# Revit family: Echo Eliminator - Ceiling Baffles
name_source: partatom
category: Specialty Equipment
units: mm (PartAtom-declared; Revit-internal decimal feet)

## family parameters
Always vertical = Yes
Cut with Voids When Loaded = No
Enable Cutting in Views = Yes
Maintain Annotation Orientation = No
OmniClass Number = 23.35.00.00
OmniClass Title = Covering, Cladding, and Finishes
Part Type = Normal
Room Calculation Point = No
Round Connector Dimension = Use Diameter
Shared = No
Work Plane-Based = No

## types (46) — shared parameters
Acoustics - NRC = Sound absorption varies from NRC 0.45 to 0.95 based on installation method used when tested per ASTM C423.
Assembly Code = C30
Default Elevation = 0' - 0"
Description = Acoustic Panels
Fire Rating = ASTM E84 - Class A
Manufacturer = Acoustical Surfaces, Inc.
Material = Echo Eliminator
Model = Echo Eliminator - Baffles
Recycled Content Percentage = 0%
Type Comments = Acoustic panels for ceiling
URL = https://www.acousticalsurfaces.com

## per-type parameters (varying)
| type | B | Finish | Length | T | Thickness Options | Width | ‍      1. Thickness 1" | ‍      2. Thickness 2" |
| 24 x 48 - 1 INCH - Black | 1' - 0" | Paint - Acoustical-Surfaces - Echo Eliminator - Black | 4' - 0" | 0' - 1" | 1 | 2' - 0" | Yes | No |
| 24 x 48 - 1 INCH - Charcoal | 1' - 0" | Paint - Acoustical-Surfaces - Echo Eliminator - Charcoal | 4' - 0" | 0' - 1" | 1 | 2' - 0" | Yes | No |
| 24 x 48 - 1 INCH - Gray | 1' - 0" | Paint - Acoustical-Surfaces - Echo Eliminator - Grey | 4' - 0" | 0' - 1" | 1 | 2' - 0" | Yes | No |
| 24 x 48 - 1 INCH - Marble Blue | 1' - 0" | Paint - Acoustical-Surfaces - Echo Eliminator - Marble Blue | 4' - 0" | 0' - 1" | 1 | 2' - 0" | Yes | No |
| 24 x 48 - 1 INCH - Beige | 1' - 0" | Paint - Acoustical-Surfaces - Echo Eliminator - Beige | 4' - 0" | 0' - 1" | 1 | 2' - 0" | Yes | No |
| 24 x 48 - 1 INCH - White | 1' - 0" | Paint - Acoustical-Surfaces - Echo Eliminator - White | 4' - 0" | 0' - 1" | 1 | 2' - 0" | Yes | No |
| 48 x 96 - 2 INCH - Black | 2' - 0" | Paint - Acoustical-Surfaces - Echo Eliminator - Black | 8' - 0" | 0' - 2" | 2 | 4' - 0" | No | Yes |
| 48 x 96 - 2 INCH - Charcoal | 2' - 0" | Paint - Acoustical-Surfaces - Echo Eliminator - Charcoal | 8' - 0" | 0' - 2" | 2 | 4' - 0" | No | Yes |
| 48 x 96 - 2 INCH - Marble Blue | 2' - 0" | Paint - Acoustical-Surfaces - Echo Eliminator - Marble Blue | 8' - 0" | 0' - 2" | 2 | 4' - 0" | No | Yes |
| 48 x 96 - 2 INCH - Beige | 2' - 0" | Paint - Acoustical-Surfaces - Echo Eliminator - Beige | 8' - 0" | 0' - 2" | 2 | 4' - 0" | No | Yes |
| 48 x 96 - 2 INCH - White | 2' - 0" | Paint - Acoustical-Surfaces - Echo Eliminator - White | 8' - 0" | 0' - 2" | 2 | 4' - 0" | No | Yes |
| 48 x 96 - 1 INCH - Black | 2' - 0" | Paint - Acoustical-Surfaces - Echo Eliminator - Black | 8' - 0" | 0' - 1" | 1 | 4' - 0" | Yes | No |
| 48 x 96 - 1 INCH - Charcoal | 2' - 0" | Paint - Acoustical-Surfaces - Echo Eliminator - Charcoal | 8' - 0" | 0' - 1" | 1 | 4' - 0" | Yes | No |
| 48 x 96 - 1 INCH - Marble Blue | 2' - 0" | Paint - Acoustical-Surfaces - Echo Eliminator - Marble Blue | 8' - 0" | 0' - 1" | 1 | 4' - 0" | Yes | No |
| 48 x 96 - 1 INCH - Beige | 2' - 0" | Paint - Acoustical-Surfaces - Echo Eliminator - Beige | 8' - 0" | 0' - 1" | 1 | 4' - 0" | Yes | No |
| 48 x 96 - 1 INCH - White | 2' - 0" | Paint - Acoustical-Surfaces - Echo Eliminator - White | 8' - 0" | 0' - 1" | 1 | 4' - 0" | Yes | No |
| 48 x 48 - 2 INCH - Black | 2' - 0" | Paint - Acoustical-Surfaces - Echo Eliminator - Black | 4' - 0" | 0' - 2" | 2 | 4' - 0" | No | Yes |
| 48 x 48 - 2 INCH - Charcoal | 2' - 0" | Paint - Acoustical-Surfaces - Echo Eliminator - Charcoal | 4' - 0" | 0' - 2" | 2 | 4' - 0" | No | Yes |
| 48 x 48 - 2 INCH - Gray | 2' - 0" | Paint - Acoustical-Surfaces - Echo Eliminator - Grey | 4' - 0" | 0' - 2" | 2 | 4' - 0" | No | Yes |
| 48 x 48 - 2 INCH - Marble Blue | 2' - 0" | Paint - Acoustical-Surfaces - Echo Eliminator - Marble Blue | 4' - 0" | 0' - 2" | 2 | 4' - 0" | No | Yes |
| 48 x 48 - 2 INCH - Beige | 2' - 0" | Paint - Acoustical-Surfaces - Echo Eliminator - Beige | 4' - 0" | 0' - 2" | 2 | 4' - 0" | No | Yes |
| 48 x 48 - 2 INCH - White | 2' - 0" | Paint - Acoustical-Surfaces - Echo Eliminator - White | 4' - 0" | 0' - 2" | 2 | 4' - 0" | No | Yes |
| 48 x 48 - 1 INCH - Black | 2' - 0" | Paint - Acoustical-Surfaces - Echo Eliminator - Black | 4' - 0" | 0' - 1" | 1 | 4' - 0" | Yes | No |
| 48 x 48 - 1 INCH - Charcoal | 2' - 0" | Paint - Acoustical-Surfaces - Echo Eliminator - Charcoal | 4' - 0" | 0' - 1" | 1 | 4' - 0" | Yes | No |
| 48 x 48 - 1 INCH - Gray | 2' - 0" | Paint - Acoustical-Surfaces - Echo Eliminator - Grey | 4' - 0" | 0' - 1" | 1 | 4' - 0" | Yes | No |
| 48 x 48 - 1 INCH - Marble Blue | 2' - 0" | Paint - Acoustical-Surfaces - Echo Eliminator - Marble Blue | 4' - 0" | 0' - 1" | 1 | 4' - 0" | Yes | No |
| 48 x 48 - 1 INCH - Beige | 2' - 0" | Paint - Acoustical-Surfaces - Echo Eliminator - Beige | 4' - 0" | 0' - 1" | 1 | 4' - 0" | Yes | No |
| 48 x 48 - 1 INCH - White | 2' - 0" | Paint - Acoustical-Surfaces - Echo Eliminator - White | 4' - 0" | 0' - 1" | 1 | 4' - 0" | Yes | No |
| 24 x 24 - 2 INCH - Black | 1' - 0" | Paint - Acoustical-Surfaces - Echo Eliminator - Black | 2' - 0" | 0' - 2" | 2 | 2' - 0" | No | Yes |
| 24 x 24 - 2 INCH - Charcoal | 1' - 0" | Paint - Acoustical-Surfaces - Echo Eliminator - Charcoal | 2' - 0" | 0' - 2" | 2 | 2' - 0" | No | Yes |
| 24 x 24 - 2 INCH - Gray | 1' - 0" | Paint - Acoustical-Surfaces - Echo Eliminator - Grey | 2' - 0" | 0' - 2" | 2 | 2' - 0" | No | Yes |
| 24 x 24 - 2 INCH - Marble Blue | 1' - 0" | Paint - Acoustical-Surfaces - Echo Eliminator - Marble Blue | 2' - 0" | 0' - 2" | 2 | 2' - 0" | No | Yes |
| 24 x 24 - 2 INCH - Beige | 1' - 0" | Paint - Acoustical-Surfaces - Echo Eliminator - Beige | 2' - 0" | 0' - 2" | 2 | 2' - 0" | No | Yes |
| 24 x 24 - 2 INCH - White | 1' - 0" | Paint - Acoustical-Surfaces - Echo Eliminator - White | 2' - 0" | 0' - 2" | 2 | 2' - 0" | No | Yes |
| 24 x 24 - 1 INCH - Black | 1' - 0" | Paint - Acoustical-Surfaces - Echo Eliminator - Black | 2' - 0" | 0' - 1" | 1 | 2' - 0" | Yes | No |
| 24 x 24 - 1 INCH - Charcoal | 1' - 0" | Paint - Acoustical-Surfaces - Echo Eliminator - Charcoal | 2' - 0" | 0' - 1" | 1 | 2' - 0" | Yes | No |
| 24 x 24 - 1 INCH - Gray | 1' - 0" | Paint - Acoustical-Surfaces - Echo Eliminator - Grey | 2' - 0" | 0' - 1" | 1 | 2' - 0" | Yes | No |
| 24 x 24 - 1 INCH - Marble Blue | 1' - 0" | Paint - Acoustical-Surfaces - Echo Eliminator - Marble Blue | 2' - 0" | 0' - 1" | 1 | 2' - 0" | Yes | No |
| 24 x 24 - 1 INCH - Beige | 1' - 0" | Paint - Acoustical-Surfaces - Echo Eliminator - Beige | 2' - 0" | 0' - 1" | 1 | 2' - 0" | Yes | No |
| 24 x 24 - 1 INCH - White | 1' - 0" | Paint - Acoustical-Surfaces - Echo Eliminator - White | 2' - 0" | 0' - 1" | 1 | 2' - 0" | Yes | No |
| 24 x 48 - 2 INCH - Black | 1' - 0" | Paint - Acoustical-Surfaces - Echo Eliminator - Black | 4' - 0" | 0' - 2" | 2 | 2' - 0" | No | Yes |
| 24 x 48 - 2 INCH - Charcoal | 1' - 0" | Paint - Acoustical-Surfaces - Echo Eliminator - Charcoal | 4' - 0" | 0' - 2" | 2 | 2' - 0" | No | Yes |
| 24 x 48 - 2 INCH - Gray | 1' - 0" | Paint - Acoustical-Surfaces - Echo Eliminator - Grey | 4' - 0" | 0' - 2" | 2 | 2' - 0" | No | Yes |
| 24 x 48 - 2 INCH - Marble Blue | 1' - 0" | Paint - Acoustical-Surfaces - Echo Eliminator - Marble Blue | 4' - 0" | 0' - 2" | 2 | 2' - 0" | No | Yes |
| 24 x 48 - 2 INCH - Beige | 1' - 0" | Paint - Acoustical-Surfaces - Echo Eliminator - Beige | 4' - 0" | 0' - 2" | 2 | 2' - 0" | No | Yes |
| 24 x 48 - 2 INCH - White | 1' - 0" | Paint - Acoustical-Surfaces - Echo Eliminator - White | 4' - 0" | 0' - 2" | 2 | 2' - 0" | No | Yes |

## geometry (parser evidence)
native form markers: Sweep x7
no freeform markers — native parametric forms only
